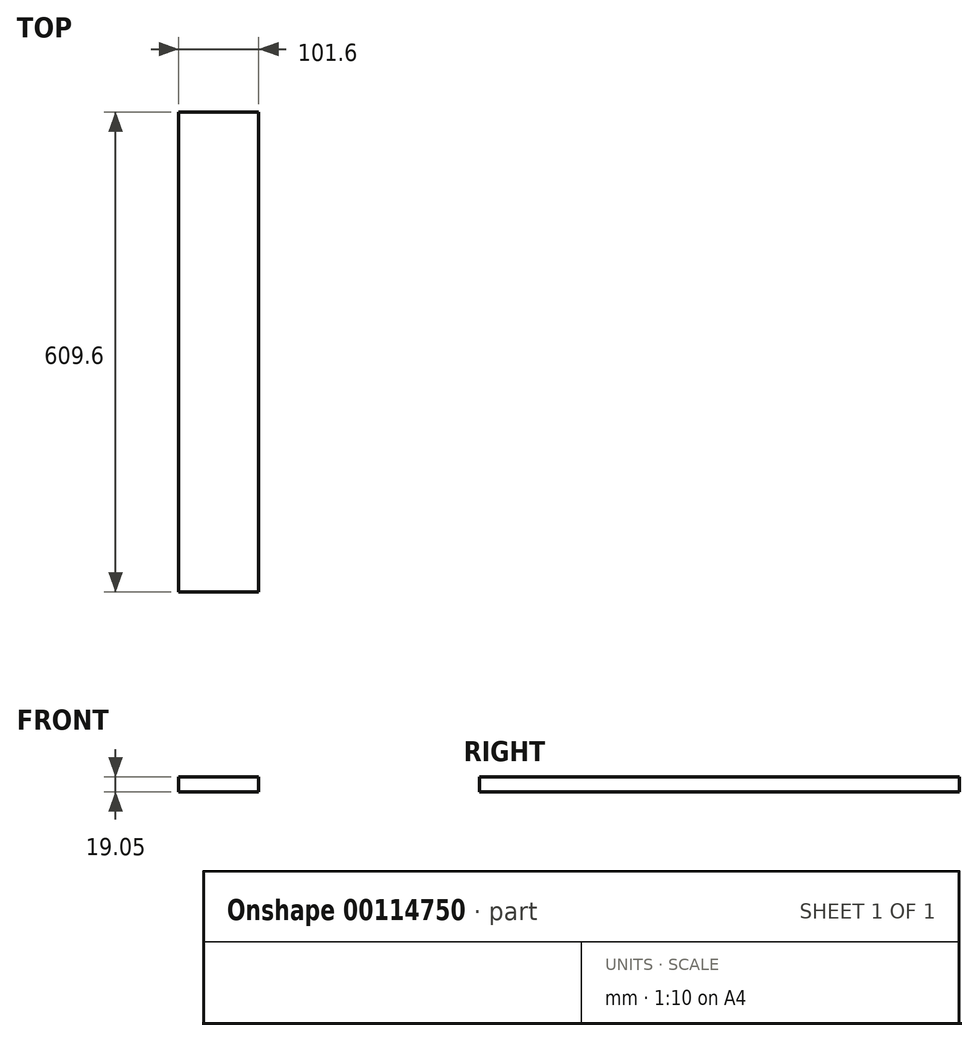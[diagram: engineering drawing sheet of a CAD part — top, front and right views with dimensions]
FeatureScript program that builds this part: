
annotation { "Feature Type Name" : "Feature", "Feature Type Description" : "" }
export const myFeature = defineFeature(function(context is Context, id is Id, definition is map)
    precondition{}
    {
        {
            var Q0;
            Q0=qCreatedBy(makeId("Top.planeOp"),FACE);
            var sketch = newSketch(context, id + "F0", { "sketchPlane" : qUnion([Q0])});
            skLineSegment(sketch, "E0.bottom", {"start": v(0, 0) * mm, "end": v(101.6, 0) * mm});
            skLineSegment(sketch, "E0.top", {"start": v(0, 609.6) * mm, "end": v(101.6, 609.6) * mm});
            skLineSegment(sketch, "E0.left", {"start": v(0, 0) * mm, "end": v(0, 609.6) * mm});
            skLineSegment(sketch, "E0.right", {"start": v(101.6, 0) * mm, "end": v(101.6, 609.6) * mm});
            skSolve(sketch);
        }
        {
            var Q0;
            Q0=qSketchRegion(id+"F0",true);
            extrude(context, id + "F1", {"entities" : qUnion([Q0]), "depth" : 19.05 * mm});
        }
    });
